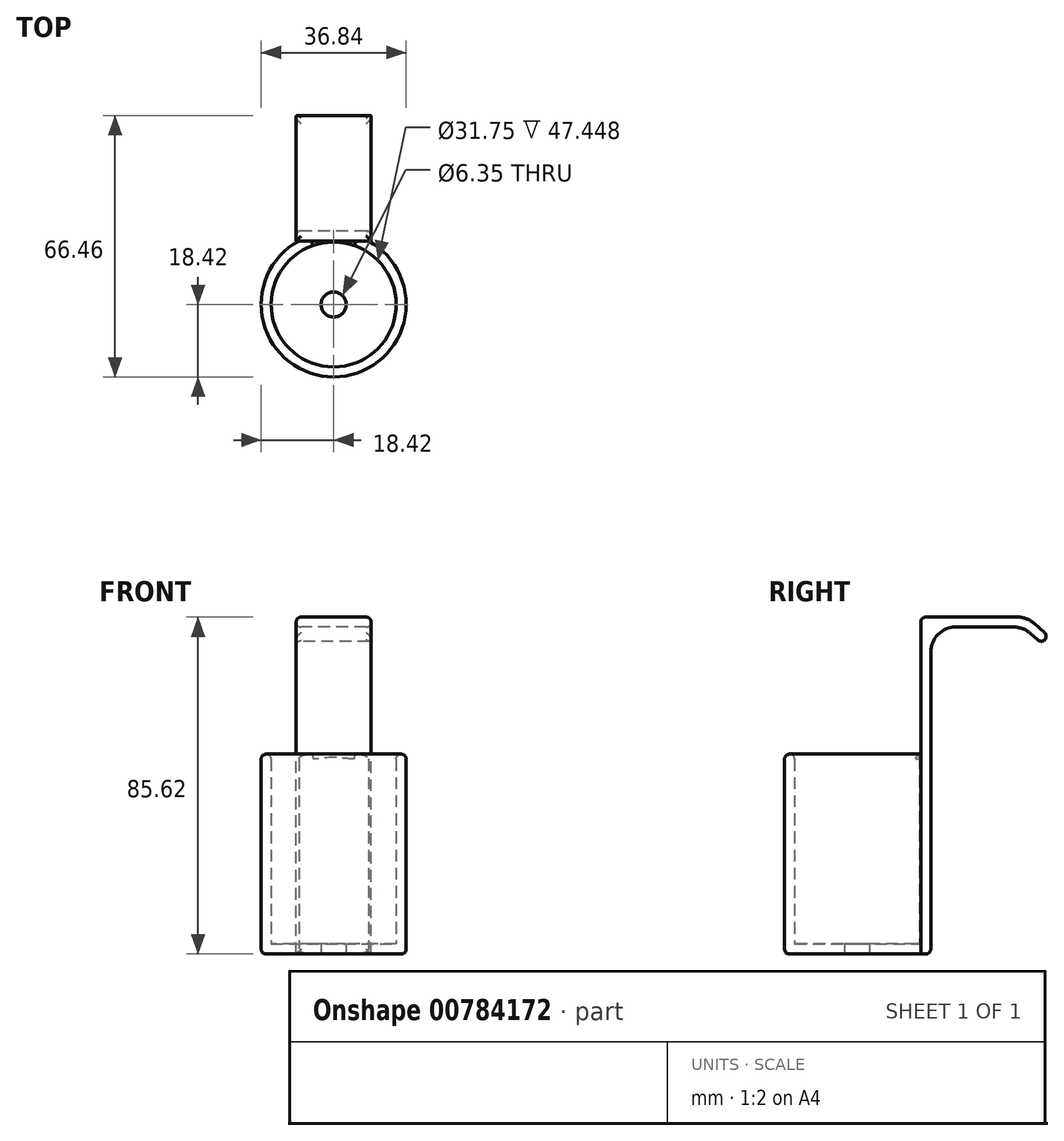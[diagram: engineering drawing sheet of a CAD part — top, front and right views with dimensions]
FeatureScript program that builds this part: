
annotation { "Feature Type Name" : "Feature", "Feature Type Description" : "" }
export const myFeature = defineFeature(function(context is Context, id is Id, definition is map)
    precondition{}
    {
        {
            var Q0;
            Q0=qCreatedBy(makeId("Top.planeOp"),FACE);
            var sketch = newSketch(context, id + "F0", { "sketchPlane" : qUnion([Q0])});
            skCircle(sketch, "E0", {"center": v(0, 0) * mm, "radius": 18.41 * mm});
            skSolve(sketch);
        }
        {
            var Q0;
            Q0 = qSketchRegion(id + "F0", true);
            extrude(context, id + "F1", {"entities" : qUnion([Q0]), "depth" : 50.8 * mm, "offsetDistance" : 25.4 * mm});
        }
        {
            var Q0;
            Q0=makeQuery(id+"F1.opExtrude","CAP_FACE",FACE,{"disambiguationData":[OSD([sQuery(id+"F0.wireOp",EDGE,"E0")])],"isStart":false});
            shell(context, id + "F2", {"entities" : qUnion([Q0]), "thickness" : 2.54 * mm});
        }
        {
            var Q0;
            Q0=qCreatedBy(makeId("Right.planeOp"),FACE);
            var sketch = newSketch(context, id + "F3", { "sketchPlane" : qUnion([Q0])});
            skLineSegment(sketch, "E1.bottom", {"start": v(16.17, 0) * mm, "end": v(18.71, 0) * mm});
            skLineSegment(sketch, "E1.top", {"start": v(16.17, 85.62) * mm, "end": v(18.71, 85.62) * mm});
            skLineSegment(sketch, "E1.left", {"start": v(16.17, 0) * mm, "end": v(16.17, 85.62) * mm});
            skLineSegment(sketch, "E1.right", {"start": v(18.71, 0) * mm, "end": v(18.71, 76.73) * mm});
            skLineSegment(sketch, "E2", {"start": v(18.71, 85.62) * mm, "end": v(40.8, 85.62) * mm});
            skLineSegment(sketch, "E3", {"start": v(45.03, 84) * mm, "end": v(48.56, 80.84) * mm});
            skLineSegment(sketch, "E4.0", {"start": v(44.06, 81.46) * mm, "end": v(46.87, 78.94) * mm});
            skLineSegment(sketch, "E4.1", {"start": v(25.06, 83.08) * mm, "end": v(39.82, 83.08) * mm});
            skLineSegment(sketch, "E5", {"start": v(48.56, 80.84) * mm, "end": v(46.87, 78.94) * mm});
            skPoint(sketch, "E6.visualSharp", {"position": v(18.71, 83.08) * mm});
            skArc(sketch, "E6.filletArc", {"start": v(25.06, 83.08) * mm, "mid": v(20.57, 81.22) * mm, "end": v(18.71, 76.73) * mm});
            skPoint(sketch, "E7.visualSharp", {"position": v(42.25, 83.08) * mm});
            skArc(sketch, "E7.filletArc", {"start": v(44.06, 81.46) * mm, "mid": v(42.09, 82.66) * mm, "end": v(39.82, 83.08) * mm});
            skPoint(sketch, "E8.visualSharp", {"position": v(43.22, 85.62) * mm});
            skArc(sketch, "E8.filletArc", {"start": v(45.03, 84) * mm, "mid": v(43.06, 85.2) * mm, "end": v(40.8, 85.62) * mm});
            skSolve(sketch);
        }
        {
            var Q0;
            Q0 = qSketchRegion(id + "F3", true);
            extrude(context, id + "F4", {"entities" : qUnion([Q0]), "operationType" : NewBodyOperationType.ADD, "depth" : 9.52 * mm, "offsetDistance" : 25.4 * mm, "hasSecondDirection" : true, "secondDirectionOppositeDirection" : true, "secondDirectionDepth" : 9.52 * mm});
        }
        {
            var Q0;
            Q0=makeQuery(id+"F1.opExtrude","CAP_EDGE",EDGE,{"disambiguationData":[OSD([sQuery(id+"F0.wireOp",EDGE,"E0")])],"isStart":false});
            var Q1;
            {var subQ0=sQuery(id+"F0.wireOp",EDGE,"E0");Q1=makeQuery(id+"F2.opShell","OFFSET_EDGE",EDGE,{"disambiguationData":[OSD([subQ0]),TDD([makeQuery(id+"F1.opExtrude","CAP_EDGE",EDGE,{"disambiguationData":[OSD([subQ0])],"isStart":false})])]});}
            var Q2;
            Q2=makeQuery(id+"F1.opExtrude","CAP_EDGE",EDGE,{"disambiguationData":[OSD([sQuery(id+"F0.wireOp",EDGE,"E0")])],"isStart":true});
            var Q3;
            Q3=makeQuery(id+"F4.opExtrude","SWEPT_EDGE",EDGE,{"disambiguationData":[OSD([sQuery(id+"F3.wireOp",EDGE,"E1.top"),sQuery(id+"F3.wireOp",EDGE,"E1.left")])]});
            var Q4;
            Q4=makeQuery(id+"F4.opExtrude","CAP_EDGE",EDGE,{"disambiguationData":[OSD([sQuery(id+"F3.wireOp",EDGE,"E1.top"),sQuery(id+"F3.wireOp",EDGE,"E2")])],"isStart":false});
            var Q5;
            Q5=makeQuery(id+"F4.opExtrude","CAP_EDGE",EDGE,{"disambiguationData":[OSD([sQuery(id+"F3.wireOp",EDGE,"E1.top"),sQuery(id+"F3.wireOp",EDGE,"E2")])],"isStart":true});
            var Q6;
            Q6=makeQuery(id+"F4.opExtrude","CAP_EDGE",EDGE,{"disambiguationData":[OSD([sQuery(id+"F3.wireOp",EDGE,"E1.right")])],"isStart":false});
            var Q7;
            Q7=makeQuery(id+"F4.opExtrude","CAP_EDGE",EDGE,{"disambiguationData":[OSD([sQuery(id+"F3.wireOp",EDGE,"E1.right")])],"isStart":true});
            var Q8;
            Q8=makeQuery(id+"F4.opExtrude","SWEPT_EDGE",EDGE,{"disambiguationData":[OSD([sQuery(id+"F3.wireOp",EDGE,"E1.bottom"),sQuery(id+"F3.wireOp",EDGE,"E1.right")])]});
            var Q9;
            Q9=makeQuery(id+"F4.opExtrude","SWEPT_EDGE",EDGE,{"disambiguationData":[OSD([sQuery(id+"F3.wireOp",EDGE,"E3"),sQuery(id+"F3.wireOp",EDGE,"E5")])]});
            var Q10;
            Q10=makeQuery(id+"F4.opExtrude","SWEPT_EDGE",EDGE,{"disambiguationData":[OSD([sQuery(id+"F3.wireOp",EDGE,"E4.0"),sQuery(id+"F3.wireOp",EDGE,"E5")])]});
            fillet(context, id + "F5", {"entities" : qUnion([Q0, Q1, Q2, Q3, Q4, Q5, Q6, Q7, Q8, Q9, Q10]), "radius" : 1.27 * mm, "tangentPropagation" : true, "allowEdgeOverflow" : false});
        }
        {
            var Q0;
            Q0=qCreatedBy(makeId("Top.planeOp"),FACE);
            var sketch = newSketch(context, id + "F6", { "sketchPlane" : qUnion([Q0])});
            skCircle(sketch, "E9", {"center": v(0, 0) * mm, "radius": 3.18 * mm});
            skSolve(sketch);
        }
        {
            var Q0;
            Q0 = qSketchRegion(id + "F6", true);
            extrude(context, id + "F7", {"entities" : qUnion([Q0]), "operationType" : NewBodyOperationType.REMOVE, "depth" : 25.4 * mm, "offsetDistance" : 25.4 * mm});
        }
    });
